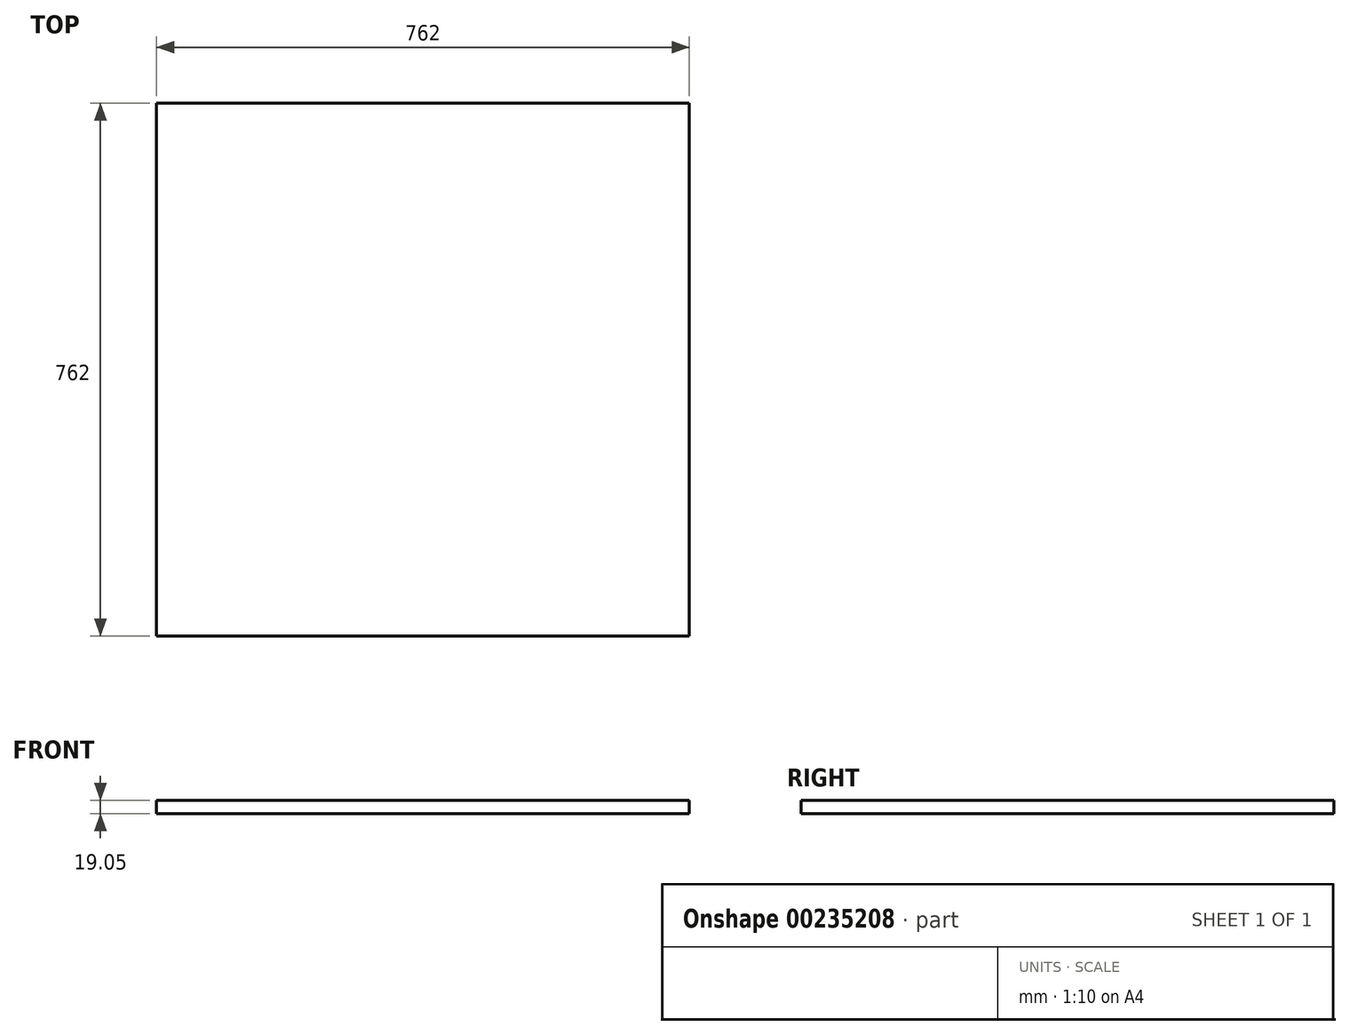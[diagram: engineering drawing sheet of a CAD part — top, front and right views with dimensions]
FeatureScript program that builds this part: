
annotation { "Feature Type Name" : "Feature", "Feature Type Description" : "" }
export const myFeature = defineFeature(function(context is Context, id is Id, definition is map)
    precondition{}
    {
        {
            var Q0;
            Q0=qCreatedBy(makeId("Top.planeOp"),FACE);
            var sketch = newSketch(context, id + "F0", { "sketchPlane" : qUnion([Q0])});
            skLineSegment(sketch, "E0.bottom", {"start": v(381, 381) * mm, "end": v(-381, 381) * mm});
            skLineSegment(sketch, "E0.top", {"start": v(381, -381) * mm, "end": v(-381, -381) * mm});
            skLineSegment(sketch, "E0.left", {"start": v(381, 381) * mm, "end": v(381, -381) * mm});
            skLineSegment(sketch, "E0.right", {"start": v(-381, 381) * mm, "end": v(-381, -381) * mm});
            skPoint(sketch, "E0.middle", {"position": v(0, 0) * mm});
            skSolve(sketch);
        }
        {
            var Q0;
            Q0=makeQuery(id+"F0.imprint","IMPRINT",FACE,{"disambiguationData":[TD([[makeQuery(id+"F0.imprint","IMPRINT",EDGE,{"derivedFrom":sQuery(id+"F0.wireOp",EDGE,"E0.bottom")}),1.0]])]});
            extrude(context, id + "F1", {"entities" : qUnion([Q0]), "depth" : 19.05 * mm});
        }
    });
